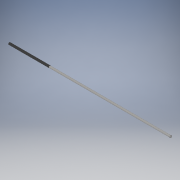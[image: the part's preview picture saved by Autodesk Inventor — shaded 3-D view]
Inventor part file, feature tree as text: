
AUTODESK INVENTOR PART (.ipt)
format: ipt  version: 2019 (Build 230136000, 136)  size: 1,552,384 bytes
history: native  units: mm
features: extrude x1, thread x1, sketch x1, mirror x1
ambient origin geometry x8: Origin, YZ Plane, XZ Plane, XY Plane, X Axis, Y Axis, Z Axis, Center Point
bodies: Solid1 (feature_tree)
feature tree (4):
  extrude  "Extrusion1"  Depth=225.0mm TaperAngle=0.0deg
  thread  "Thread1"  [1 undecoded]
  sketch  "Sketch1"  dims[d0=3.65mm d1=225.0mm d2=0.0mm d3=10.0mm d4=0.0mm]
  mirror  "Mirror1"
note: 1 required parameter value undecoded (feature->parameter linkage not recoverable at this tier; creation-order binding heuristic only, values carry confidence <= 0.55)
